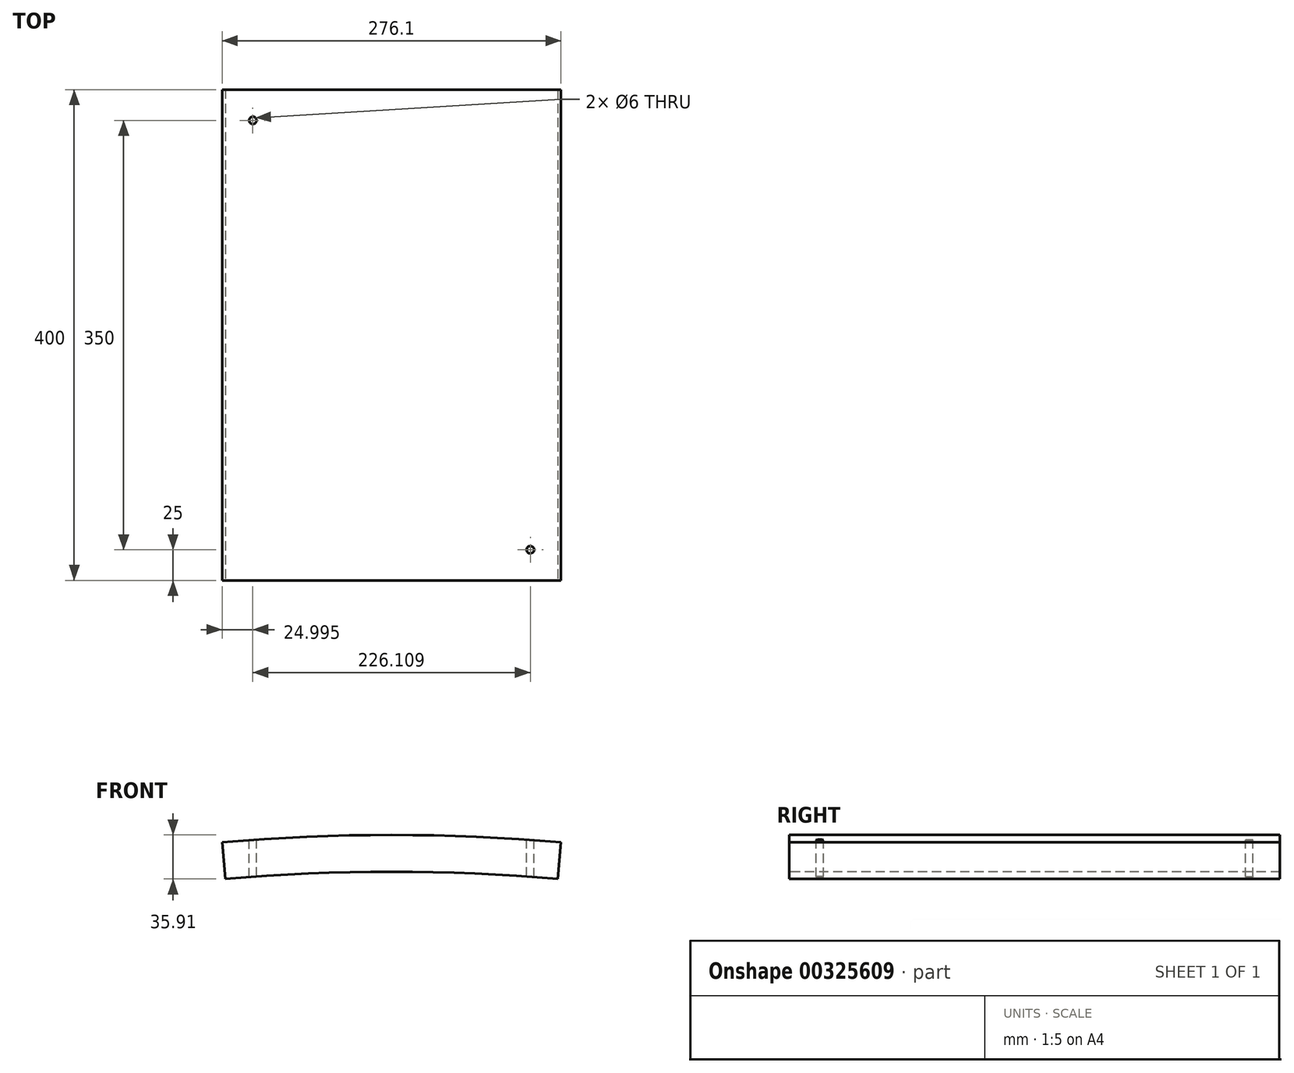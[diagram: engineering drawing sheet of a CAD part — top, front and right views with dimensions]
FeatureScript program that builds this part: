
annotation { "Feature Type Name" : "Feature", "Feature Type Description" : "" }
export const myFeature = defineFeature(function(context is Context, id is Id, definition is map)
    precondition{}
    {
        {
            var Q0;
            Q0=qCreatedBy(makeId("Right.planeOp"),FACE);
            var sketch = newSketch(context, id + "F0", { "sketchPlane" : qUnion([Q0])});
            skLineSegment(sketch, "E0", {"start": v(-75.2, 0) * mm, "end": v(74.8, 0) * mm, "construction": true});
            skLineSegment(sketch, "E1.bottom", {"start": v(200, 1554) * mm, "end": v(-200, 1554) * mm});
            skLineSegment(sketch, "E1.top", {"start": v(200, 1584) * mm, "end": v(-200, 1584) * mm});
            skLineSegment(sketch, "E1.left", {"start": v(200, 1554) * mm, "end": v(200, 1584) * mm});
            skLineSegment(sketch, "E1.right", {"start": v(-200, 1554) * mm, "end": v(-200, 1584) * mm});
            skPoint(sketch, "E1.middle", {"position": v(0, 1569) * mm});
            skSolve(sketch);
        }
        {
            var Q0;
            Q0=makeQuery(id+"F0.imprint","IMPRINT",FACE,{"disambiguationData":[TD([[makeQuery(id+"F0.imprint","IMPRINT",EDGE,{"derivedFrom":sQuery(id+"F0.wireOp",EDGE,"E1.bottom")}),-1.0]])]});
            var Q1;
            Q1=sQuery(id+"F0.wireOp",EDGE,"E0");
            revolve(context, id + "F1", {"entities" : qUnion([Q0]), "axis" : qUnion([Q1]), "revolveType" : RevolveType.SYMMETRIC, "angle" : 10 * degree});
        }
        {
            var Q0;
            Q0=qCreatedBy(makeId("Top.planeOp"),FACE);
            cPlane(context, id + "F2", {"entities" : qUnion([Q0]), "cplaneType" : CPlaneType.OFFSET, "offset" : 1600 * mm, "width" : 150 * mm, "height" : 150 * mm});
        }
        {
            var Q0;
            Q0=qCreatedBy(id+"F2.planeOp",FACE);
            var sketch = newSketch(context, id + "F3", { "sketchPlane" : qUnion([Q0])});
            skCircle(sketch, "E2", {"center": v(-113.05, 175) * mm, "radius": 3 * mm});
            skLineSegment(sketch, "E3", {"start": v(150.49, 0) * mm, "end": v(-149.91, 0) * mm, "construction": true});
            skLineSegment(sketch, "E4", {"start": v(0, 158.55) * mm, "end": v(0, -163.66) * mm, "construction": true});
            skPoint(sketch, "E5", {"position": v(0, 0) * mm});
            skCircle(sketch, "E6", {"center": v(113.05, -175) * mm, "radius": 3 * mm});
            skSolve(sketch);
        }
        {
            var Q0;
            Q0=sQuery(id+"F3.wireOp",VERTEX,"E2.center");
            var Q1;
            Q1=sQuery(id+"F3.wireOp",VERTEX,"E6.center");
            var Q2;
            Q2=makeQuery(id+"F1.opRevolve","SWEPT_BODY",BODY,{"disambiguationData":[OSD([sQuery(id+"F0.wireOp",EDGE,"E1.bottom"),sQuery(id+"F0.wireOp",EDGE,"E1.top"),sQuery(id+"F0.wireOp",EDGE,"E1.left"),sQuery(id+"F0.wireOp",EDGE,"E1.right")])]});
            hole(context, id + "F4", {"style" : HoleStyle.SIMPLE, "endStyle" : HoleEndStyle.BLIND, "holeDiameter" : 6 * mm, "holeDepth" : 100 * mm, "tappedDepth" : 12 * mm, "tapClearance" : 3, "startFromSketch" : true, "locations" : qUnion([Q0, Q1]), "scope" : qUnion([Q2])});
        }
    });
